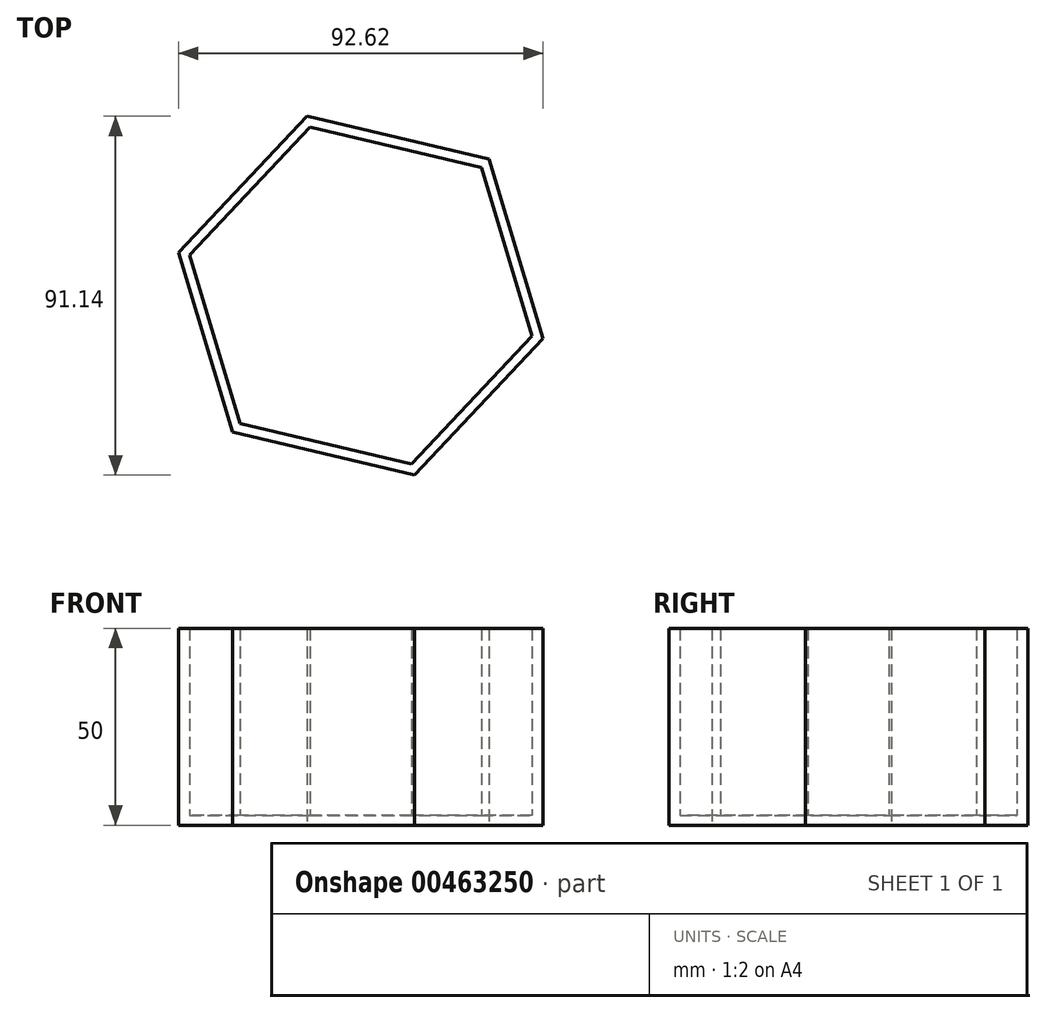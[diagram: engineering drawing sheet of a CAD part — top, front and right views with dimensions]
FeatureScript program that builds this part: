
annotation { "Feature Type Name" : "Feature", "Feature Type Description" : "" }
export const myFeature = defineFeature(function(context is Context, id is Id, definition is map)
    precondition{}
    {
        {
            var Q0;
            Q0=qCreatedBy(makeId("Top.planeOp"),FACE);
            var sketch = newSketch(context, id + "F0", { "sketchPlane" : qUnion([Q0])});
            skCircle(sketch, "E0.cCircle", {"center": v(0, 0) * mm, "radius": 41.2 * mm, "construction": true});
            skLineSegment(sketch, "E0.0", {"start": v(-46.3, 10.93) * mm, "end": v(-13.7, 45.57) * mm});
            skLineSegment(sketch, "E0.1", {"start": v(-13.7, 45.57) * mm, "end": v(32.62, 34.64) * mm});
            skLineSegment(sketch, "E0.2", {"start": v(32.62, 34.64) * mm, "end": v(46.3, -10.93) * mm});
            skLineSegment(sketch, "E0.3", {"start": v(46.3, -10.93) * mm, "end": v(13.7, -45.57) * mm});
            skLineSegment(sketch, "E0.4", {"start": v(13.7, -45.57) * mm, "end": v(-32.62, -34.64) * mm});
            skLineSegment(sketch, "E0.5", {"start": v(-32.62, -34.64) * mm, "end": v(-46.3, 10.93) * mm});
            skPoint(sketch, "E0.0.midPoint", {"position": v(-30, 28.25) * mm});
            skSolve(sketch);
        }
        {
            var Q0;
            Q0=makeQuery(id+"F0.imprint","IMPRINT",FACE,{"disambiguationData":[TD([[makeQuery(id+"F0.imprint","IMPRINT",EDGE,{"derivedFrom":sQuery(id+"F0.wireOp",EDGE,"E0.0")}),-1.0]])]});
            extrude(context, id + "F1", {"entities" : qUnion([Q0]), "depth" : 50 * mm, "offsetDistance" : 25 * mm});
        }
        {
            var Q0;
            Q0=makeQuery(id+"F1.opExtrude","CAP_FACE",FACE,{"disambiguationData":[OSD([sQuery(id+"F0.wireOp",EDGE,"E0.0"),sQuery(id+"F0.wireOp",EDGE,"E0.1"),sQuery(id+"F0.wireOp",EDGE,"E0.2"),sQuery(id+"F0.wireOp",EDGE,"E0.3"),sQuery(id+"F0.wireOp",EDGE,"E0.4"),sQuery(id+"F0.wireOp",EDGE,"E0.5")])],"isStart":false});
            shell(context, id + "F2", {"entities" : qUnion([Q0]), "thickness" : 2.5 * mm});
        }
    });
